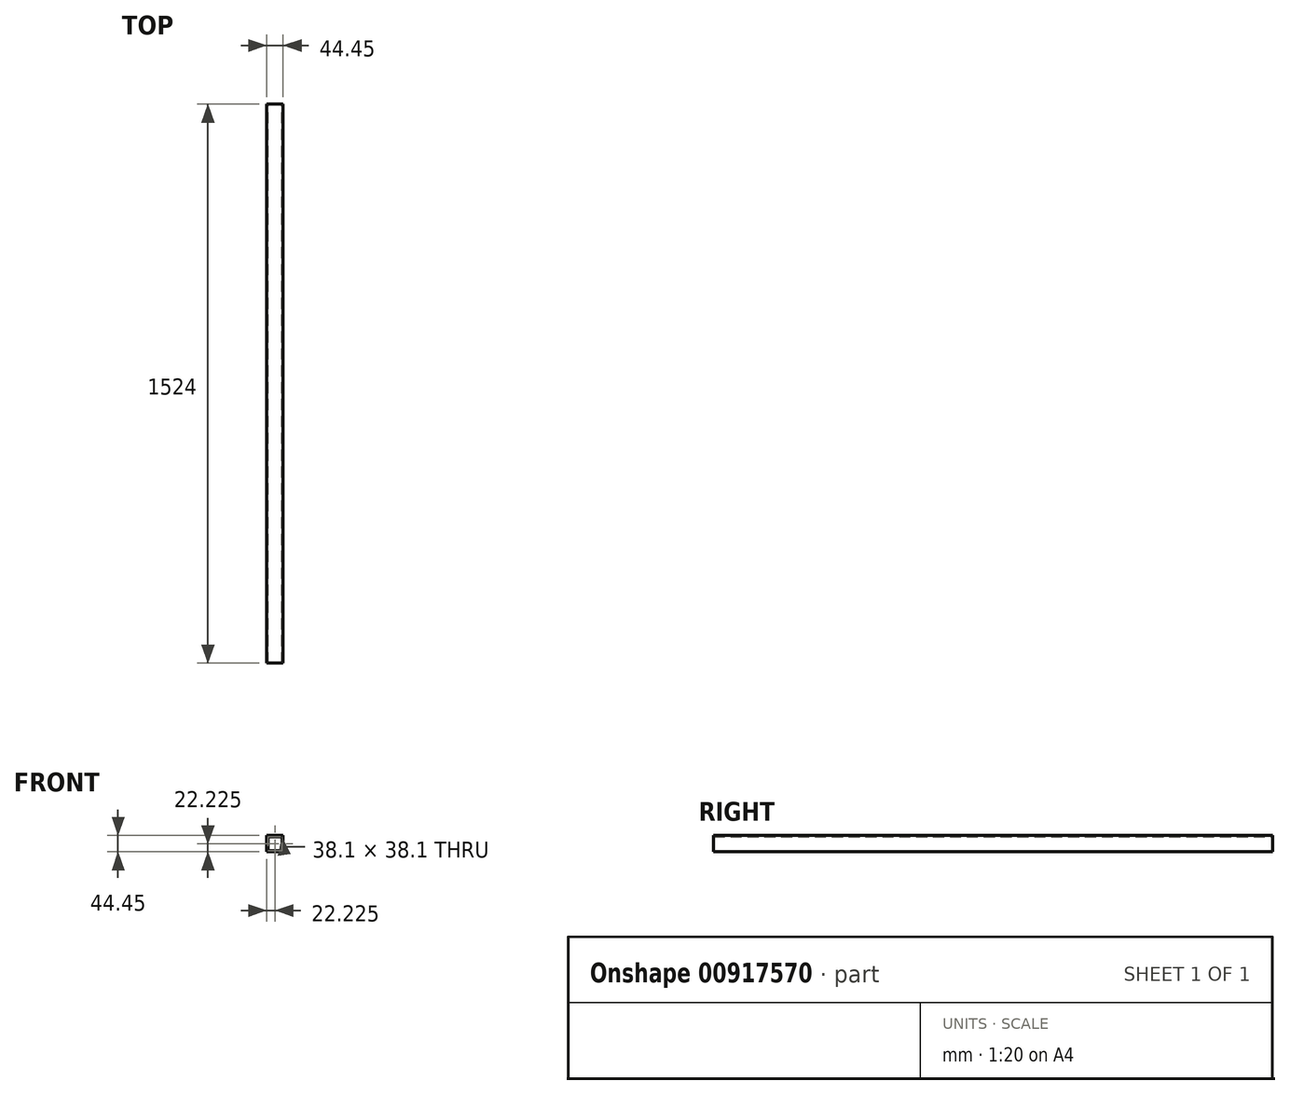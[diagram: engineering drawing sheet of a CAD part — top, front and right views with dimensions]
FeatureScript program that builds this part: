
annotation { "Feature Type Name" : "Feature", "Feature Type Description" : "" }
export const myFeature = defineFeature(function(context is Context, id is Id, definition is map)
    precondition{}
    {
        {
            var Q0;
            Q0=qCreatedBy(makeId("Front.planeOp"),FACE);
            var sketch = newSketch(context, id + "F0", { "sketchPlane" : qUnion([Q0])});
            skLineSegment(sketch, "E0.bottom", {"start": v(0, 0) * mm, "end": v(44.45, 0) * mm});
            skLineSegment(sketch, "E0.top", {"start": v(0, 44.45) * mm, "end": v(44.45, 44.45) * mm});
            skLineSegment(sketch, "E0.left", {"start": v(0, 0) * mm, "end": v(0, 44.45) * mm});
            skLineSegment(sketch, "E0.right", {"start": v(44.45, 0) * mm, "end": v(44.45, 44.45) * mm});
            skLineSegment(sketch, "E1.0", {"start": v(3.17, 41.28) * mm, "end": v(41.27, 41.28) * mm});
            skLineSegment(sketch, "E1.1", {"start": v(3.17, 3.17) * mm, "end": v(3.17, 41.28) * mm});
            skLineSegment(sketch, "E1.2", {"start": v(3.17, 3.17) * mm, "end": v(41.28, 3.17) * mm});
            skLineSegment(sketch, "E1.3", {"start": v(41.28, 3.17) * mm, "end": v(41.27, 41.28) * mm});
            skSolve(sketch);
        }
        {
            var Q0;
            Q0=makeQuery(id+"F0.imprint","IMPRINT",FACE,{"disambiguationData":[TD([[makeQuery(id+"F0.imprint","IMPRINT",EDGE,{"derivedFrom":sQuery(id+"F0.wireOp",EDGE,"E0.bottom")}),1.0]])]});
            extrude(context, id + "F1", {"entities" : qUnion([Q0]), "depth" : 1524 * mm, "offsetDistance" : 25.4 * mm});
        }
    });
